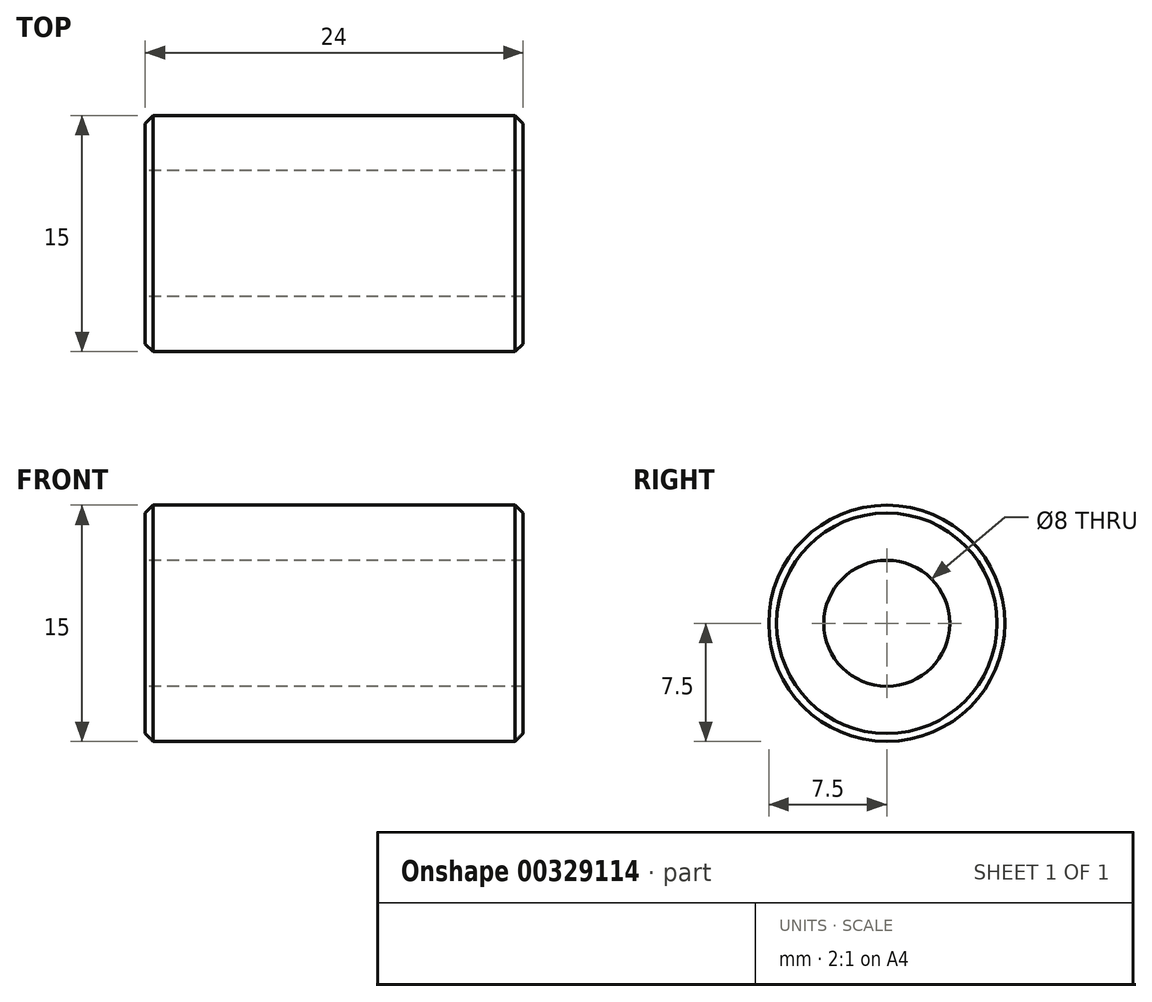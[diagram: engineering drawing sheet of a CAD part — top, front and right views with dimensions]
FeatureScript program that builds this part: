
annotation { "Feature Type Name" : "Feature", "Feature Type Description" : "" }
export const myFeature = defineFeature(function(context is Context, id is Id, definition is map)
    precondition{}
    {
        {
            var Q0;
            Q0=qCreatedBy(makeId("Right.planeOp"),FACE);
            var sketch = newSketch(context, id + "F0", { "sketchPlane" : qUnion([Q0])});
            skCircle(sketch, "E0", {"center": v(0, 0) * mm, "radius": 4 * mm});
            skCircle(sketch, "E1", {"center": v(0, 0) * mm, "radius": 7.5 * mm});
            skSolve(sketch);
        }
        {
            var Q0;
            Q0 = qSketchRegion(id + "F0", true);
            extrude(context, id + "F1", {"entities" : qUnion([Q0]), "depth" : 24 * mm});
        }
        {
            var Q0;
            Q0=makeQuery(id+"F1.opExtrude","CAP_EDGE",EDGE,{"disambiguationData":[OSD([sQuery(id+"F0.wireOp",EDGE,"E1")])],"isStart":true});
            var Q1;
            Q1=makeQuery(id+"F1.opExtrude","CAP_EDGE",EDGE,{"disambiguationData":[OSD([sQuery(id+"F0.wireOp",EDGE,"E1")])],"isStart":false});
            chamfer(context, id + "F2", {"entities" : qUnion([Q0, Q1]), "width" : 0.5 * mm, "tangentPropagation" : true});
        }
    });
